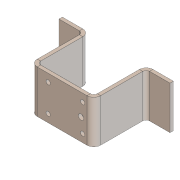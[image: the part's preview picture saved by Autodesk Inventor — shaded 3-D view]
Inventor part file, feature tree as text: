
AUTODESK INVENTOR PART (.ipt)
format: ipt  version: 2016 (Build 200138000, 138)  size: 139,776 bytes
history: native  units: in
note: dims shown in document units (in); Inventor stores cm internally (conversion verified against a paired STEP export)
features: sheet_metal_op x7, sketch x3, other x3
ambient origin geometry x8: Origin, YZ Plane, XZ Plane, XY Plane, X Axis, Y Axis, Z Axis, Center Point
bodies: Solid1 (feature_tree)
feature tree (13):
  sheet_metal_op  "Face1"
  sheet_metal_op  "Flange3"
  sheet_metal_op  "Flange4"
  sketch  "Sketch1"  dims[d2=1.5748in]
  other  "Plate1"
  sketch  "Sketch4"  dims[d3=1.8238in]
  other  "Plate4"
  sheet_metal_op  "Bend3"
  sheet_metal_op  "Corner3"
  sketch  "Sketch5"  dims[d4=0.125in d25=0.125in d26=0.0625in d27=0.25in d28=0.125in d29=2.045in d30=90.0deg d31=0.125in d32=0.5in d33=0.125in d34=0.125in d35=0.125in d36=0.0625in d37=0.25in d38=0.125in d39=1.0in d40=90.0deg d41=0.125in d42=0.5in d43=0.125in d44=0.125in]
  other  "Plate5"
  sheet_metal_op  "Bend4"
  sheet_metal_op  "Corner4"
